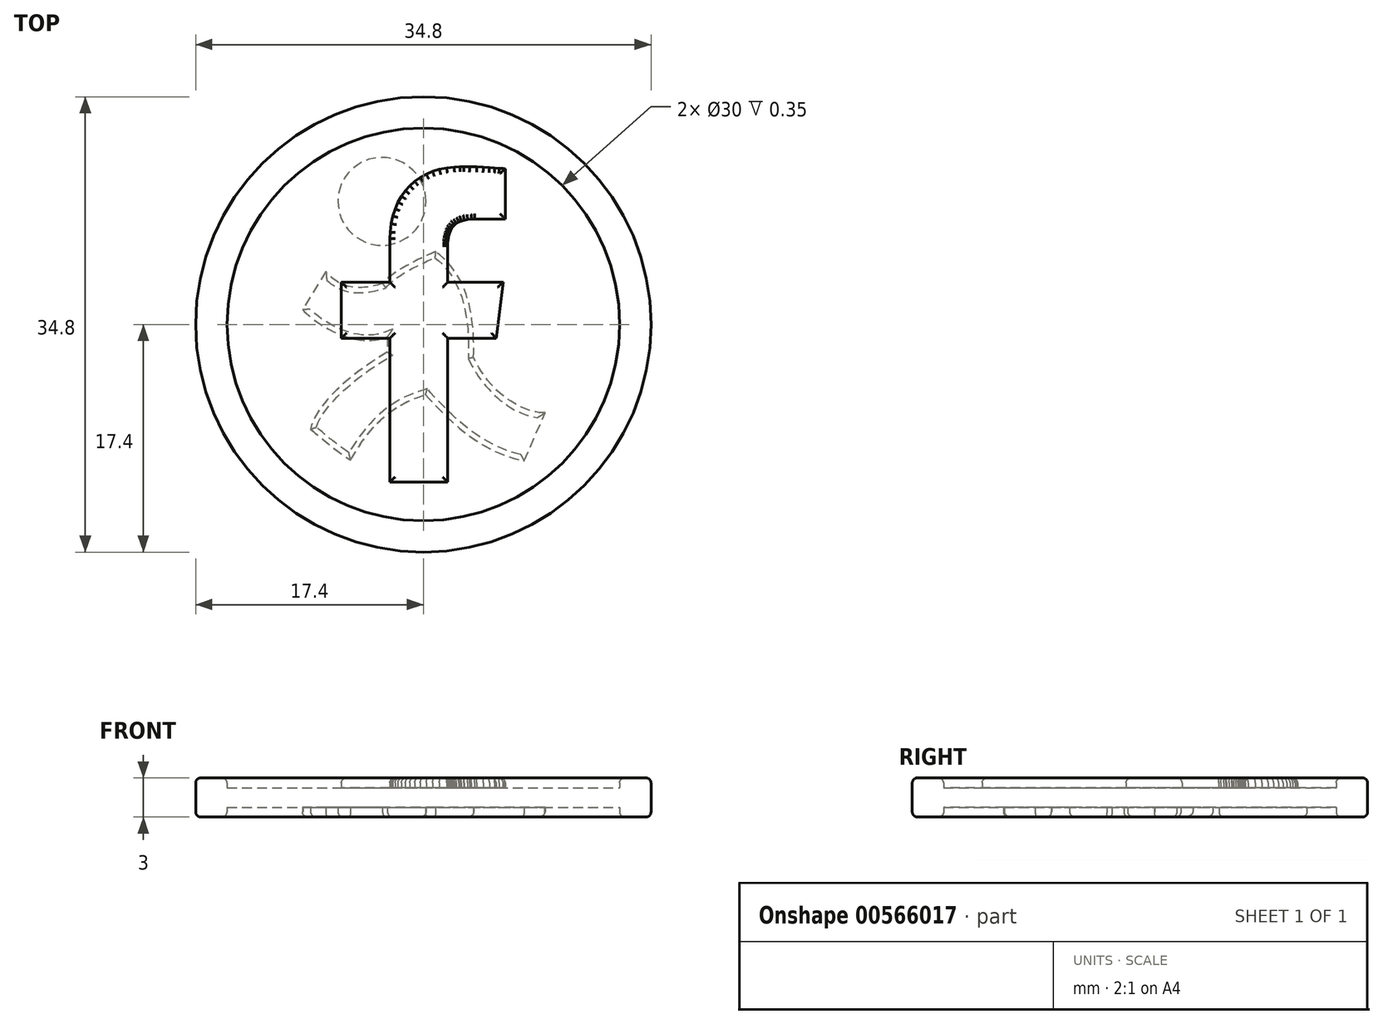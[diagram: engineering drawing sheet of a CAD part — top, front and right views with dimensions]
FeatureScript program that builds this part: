
annotation { "Feature Type Name" : "Feature", "Feature Type Description" : "" }
export const myFeature = defineFeature(function(context is Context, id is Id, definition is map)
    precondition{}
    {
        {
            var Q0;
            Q0=qCreatedBy(makeId("Front.planeOp"),FACE);
            var sketch = newSketch(context, id + "F0", { "sketchPlane" : qUnion([Q0])});
            skLineSegment(sketch, "E0", {"start": v(0, 0) * mm, "end": v(0, 0.75) * mm});
            skLineSegment(sketch, "E1", {"start": v(0, 0.75) * mm, "end": v(-15, 0.75) * mm});
            skLineSegment(sketch, "E2", {"start": v(-15, 0.75) * mm, "end": v(-17.4, 0.75) * mm});
            skLineSegment(sketch, "E3", {"start": v(-17.4, 0.75) * mm, "end": v(-17.4, 0) * mm});
            skLineSegment(sketch, "E4", {"start": v(-17.4, 0) * mm, "end": v(0, 0) * mm});
            skLineSegment(sketch, "E5", {"start": v(-15, 0.75) * mm, "end": v(-15, 0) * mm});
            skLineSegment(sketch, "E6.MirrorCS", {"start": v(0, 0) * mm, "end": v(0, -0.75) * mm});
            skLineSegment(sketch, "E7.MirrorCS", {"start": v(-15, -0.75) * mm, "end": v(-15, 0) * mm});
            skLineSegment(sketch, "E8.MirrorCS", {"start": v(-17.4, -0.75) * mm, "end": v(-17.4, 0) * mm});
            skLineSegment(sketch, "E9.MirrorCS", {"start": v(0, -0.75) * mm, "end": v(-15, -0.75) * mm});
            skLineSegment(sketch, "E10.MirrorCS", {"start": v(-15, -0.75) * mm, "end": v(-17.4, -0.75) * mm});
            skSolve(sketch);
        }
        {
            var Q0;
            {var subQ2=sQuery(id+"F0.wireOp",EDGE,"E7.MirrorCS");Q0=makeQuery(id+"F0.imprint","IMPRINT",FACE,{"disambiguationData":[TD([[makeQuery(id+"F0.imprint","IMPRINT",EDGE,{"derivedFrom":subQ2}),1.0]])]});}
            var Q1;
            Q1=makeQuery(id+"F0.imprint","IMPRINT",FACE,{"disambiguationData":[TD([[makeQuery(id+"F0.imprint","IMPRINT",EDGE,{"derivedFrom":sQuery(id+"F0.wireOp",EDGE,"E2")}),1.0]])]});
            var Q2;
            Q2=sQuery(id+"F0.wireOp",EDGE,"E0");
            revolve(context, id + "F1", {"entities" : qUnion([Q0, Q1]), "axis" : qUnion([Q2]), "revolveType" : RevolveType.FULL});
        }
        {
            var Q0;
            {var subQ0=sQuery(id+"F0.wireOp",EDGE,"E0");Q0=makeQuery(id+"F0.imprint","IMPRINT",FACE,{"disambiguationData":[TD([[makeQuery(id+"F0.imprint","IMPRINT",EDGE,{"derivedFrom":subQ0}),1.0]])]});}
            var Q1;
            {var subQ0=sQuery(id+"F0.wireOp",EDGE,"E6.MirrorCS");Q1=makeQuery(id+"F0.imprint","IMPRINT",FACE,{"disambiguationData":[TD([[makeQuery(id+"F0.imprint","IMPRINT",EDGE,{"derivedFrom":subQ0}),-1.0]])]});}
            var Q2;
            Q2=sQuery(id+"F0.wireOp",EDGE,"E0");
            revolve(context, id + "F2", {"entities" : qUnion([Q0, Q1]), "axis" : qUnion([Q2]), "revolveType" : RevolveType.FULL});
        }
        {
            var Q0;
            Q0=makeQuery(id+"F2.opRevolve","SWEPT_FACE",FACE,{"disambiguationData":[OSD([sQuery(id+"F0.wireOp",EDGE,"E1")])]});
            var sketch = newSketch(context, id + "F3", { "sketchPlane" : qUnion([Q0])});
            skLineSegment(sketch, "E11", {"start": v(1.87, -12.06) * mm, "end": v(1.87, -1.06) * mm});
            skLineSegment(sketch, "E12", {"start": v(1.87, -1.06) * mm, "end": v(5.56, -1.06) * mm});
            skLineSegment(sketch, "E13", {"start": v(5.56, -1.06) * mm, "end": v(6.11, 3.23) * mm});
            skLineSegment(sketch, "E14", {"start": v(6.11, 3.23) * mm, "end": v(1.87, 3.23) * mm});
            skLineSegment(sketch, "E15", {"start": v(1.87, 3.23) * mm, "end": v(1.87, 5.97) * mm});
            skLineSegment(sketch, "E16", {"start": v(1.87, 5.97) * mm, "end": v(1.87, 6.02) * mm});
            skLineSegment(sketch, "E17", {"start": v(1.87, 6.02) * mm, "end": v(1.87, 6.2) * mm});
            skLineSegment(sketch, "E18", {"start": v(1.87, 6.2) * mm, "end": v(1.89, 6.41) * mm});
            skLineSegment(sketch, "E19", {"start": v(1.89, 6.41) * mm, "end": v(1.91, 6.62) * mm});
            skLineSegment(sketch, "E20", {"start": v(1.91, 6.62) * mm, "end": v(1.95, 6.82) * mm});
            skLineSegment(sketch, "E21", {"start": v(1.95, 6.82) * mm, "end": v(2, 7) * mm});
            skLineSegment(sketch, "E22", {"start": v(2, 7) * mm, "end": v(2.07, 7.17) * mm});
            skLineSegment(sketch, "E23", {"start": v(2.07, 7.17) * mm, "end": v(2.16, 7.33) * mm});
            skLineSegment(sketch, "E24", {"start": v(2.16, 7.33) * mm, "end": v(2.26, 7.48) * mm});
            skLineSegment(sketch, "E25", {"start": v(2.26, 7.48) * mm, "end": v(2.39, 7.6) * mm});
            skLineSegment(sketch, "E26", {"start": v(2.39, 7.6) * mm, "end": v(2.54, 7.72) * mm});
            skLineSegment(sketch, "E27", {"start": v(2.54, 7.72) * mm, "end": v(2.71, 7.82) * mm});
            skLineSegment(sketch, "E28", {"start": v(2.71, 7.82) * mm, "end": v(2.9, 7.9) * mm});
            skLineSegment(sketch, "E29", {"start": v(2.9, 7.9) * mm, "end": v(3.13, 7.97) * mm});
            skLineSegment(sketch, "E30", {"start": v(3.13, 7.97) * mm, "end": v(3.39, 8.01) * mm});
            skLineSegment(sketch, "E31", {"start": v(3.39, 8.01) * mm, "end": v(3.67, 8.04) * mm});
            skLineSegment(sketch, "E32", {"start": v(3.67, 8.04) * mm, "end": v(3.91, 8.05) * mm});
            skLineSegment(sketch, "E33", {"start": v(3.91, 8.05) * mm, "end": v(4, 8.05) * mm});
            skLineSegment(sketch, "E34", {"start": v(4, 8.05) * mm, "end": v(6.26, 8.05) * mm});
            skLineSegment(sketch, "E35", {"start": v(6.26, 8.05) * mm, "end": v(6.26, 11.89) * mm});
            skLineSegment(sketch, "E36", {"start": v(6.26, 11.89) * mm, "end": v(6.21, 11.9) * mm});
            skLineSegment(sketch, "E37", {"start": v(6.21, 11.9) * mm, "end": v(6.07, 11.91) * mm});
            skLineSegment(sketch, "E38", {"start": v(6.07, 11.91) * mm, "end": v(5.8, 11.94) * mm});
            skLineSegment(sketch, "E39", {"start": v(5.8, 11.94) * mm, "end": v(5.46, 11.96) * mm});
            skLineSegment(sketch, "E40", {"start": v(5.46, 11.96) * mm, "end": v(5.05, 12) * mm});
            skLineSegment(sketch, "E41", {"start": v(5.05, 12) * mm, "end": v(4.59, 12.02) * mm});
            skLineSegment(sketch, "E42", {"start": v(4.59, 12.02) * mm, "end": v(4.08, 12.04) * mm});
            skLineSegment(sketch, "E43", {"start": v(4.08, 12.04) * mm, "end": v(3.53, 12.05) * mm});
            skLineSegment(sketch, "E44", {"start": v(3.53, 12.05) * mm, "end": v(3.1, 12.06) * mm});
            skLineSegment(sketch, "E45", {"start": v(3.1, 12.06) * mm, "end": v(2.95, 12.06) * mm});
            skLineSegment(sketch, "E46", {"start": v(2.95, 12.06) * mm, "end": v(2.8, 12.06) * mm});
            skLineSegment(sketch, "E47", {"start": v(2.8, 12.06) * mm, "end": v(2.35, 12.03) * mm});
            skLineSegment(sketch, "E48", {"start": v(2.35, 12.03) * mm, "end": v(1.78, 11.96) * mm});
            skLineSegment(sketch, "E49", {"start": v(1.78, 11.96) * mm, "end": v(1.23, 11.85) * mm});
            skLineSegment(sketch, "E50", {"start": v(1.23, 11.85) * mm, "end": v(0.71, 11.69) * mm});
            skLineSegment(sketch, "E51", {"start": v(0.71, 11.69) * mm, "end": v(0.22, 11.48) * mm});
            skLineSegment(sketch, "E52", {"start": v(0.22, 11.48) * mm, "end": v(-0.23, 11.23) * mm});
            skLineSegment(sketch, "E53", {"start": v(-0.23, 11.23) * mm, "end": v(-0.65, 10.94) * mm});
            skLineSegment(sketch, "E54", {"start": v(-0.65, 10.94) * mm, "end": v(-1.03, 10.6) * mm});
            skLineSegment(sketch, "E55", {"start": v(-1.03, 10.6) * mm, "end": v(-1.37, 10.22) * mm});
            skLineSegment(sketch, "E56", {"start": v(-1.37, 10.22) * mm, "end": v(-1.68, 9.8) * mm});
            skLineSegment(sketch, "E57", {"start": v(-1.68, 9.8) * mm, "end": v(-1.94, 9.33) * mm});
            skLineSegment(sketch, "E58", {"start": v(-1.94, 9.33) * mm, "end": v(-2.16, 8.82) * mm});
            skLineSegment(sketch, "E59", {"start": v(-2.16, 8.82) * mm, "end": v(-2.33, 8.28) * mm});
            skLineSegment(sketch, "E60", {"start": v(-2.33, 8.28) * mm, "end": v(-2.46, 7.69) * mm});
            skLineSegment(sketch, "E61", {"start": v(-2.46, 7.69) * mm, "end": v(-2.53, 7.06) * mm});
            skLineSegment(sketch, "E62", {"start": v(-2.53, 7.06) * mm, "end": v(-2.56, 6.56) * mm});
            skLineSegment(sketch, "E63", {"start": v(-2.56, 6.56) * mm, "end": v(-2.56, 6.4) * mm});
            skLineSegment(sketch, "E64", {"start": v(-2.56, 6.4) * mm, "end": v(-2.56, 3.23) * mm});
            skLineSegment(sketch, "E65", {"start": v(-2.56, 3.23) * mm, "end": v(-6.26, 3.23) * mm});
            skLineSegment(sketch, "E66", {"start": v(-6.26, 3.23) * mm, "end": v(-6.26, -1.06) * mm});
            skLineSegment(sketch, "E67", {"start": v(-6.26, -1.06) * mm, "end": v(-2.56, -1.06) * mm});
            skLineSegment(sketch, "E68", {"start": v(-2.56, -1.06) * mm, "end": v(-2.56, -12.06) * mm});
            skLineSegment(sketch, "E69", {"start": v(-2.56, -12.06) * mm, "end": v(1.87, -12.06) * mm});
            skSolve(sketch);
        }
        {
            var Q0;
            Q0=makeQuery(id+"F2.opRevolve","SWEPT_FACE",FACE,{"disambiguationData":[OSD([sQuery(id+"F0.wireOp",EDGE,"E9.MirrorCS")])]});
            var sketch = newSketch(context, id + "F4", { "sketchPlane" : qUnion([Q0])});
            skFitSpline(sketch, "E70", {"points": [v(0.93, -5.57) * mm, v(-3.11, -3.13) * mm], "startDerivative": vector(-3.58, 1.6) * mm, "endDerivative": vector(-2.6, 3.06) * mm});
            skFitSpline(sketch, "E71", {"points": [v(-3.11, -3.13) * mm, v(-7.44, -4.04) * mm], "startDerivative": vector(-6.77, 2.16) * mm, "endDerivative": vector(-2.52, -3.04) * mm});
            skFitSpline(sketch, "E72", {"points": [v(-7.44, -4.04) * mm, v(-9.24, -1.13) * mm], "startDerivative": vector(-1.8, 2.9) * mm, "endDerivative": vector(-1.8, 2.9) * mm});
            skFitSpline(sketch, "E73", {"points": [v(-9.2, -1.1) * mm, v(-2.74, 0.94) * mm], "startDerivative": vector(2.37, 2.47) * mm, "endDerivative": vector(8.3, -3.22) * mm});
            skPoint(sketch, "E74", {"position": v(-8.25, -0.28) * mm});
            skFitSpline(sketch, "E75", {"points": [v(-2.74, 0.94) * mm, v(-2.74, 2.12) * mm], "startDerivative": vector(0, 1.18) * mm, "endDerivative": vector(0, 1.18) * mm});
            skFitSpline(sketch, "E76", {"points": [v(-2.74, 2.12) * mm, v(-8.62, 8) * mm], "startDerivative": vector(-6.87, 3.99) * mm, "endDerivative": vector(-1.37, 6.4) * mm});
            skFitSpline(sketch, "E77", {"points": [v(-8.62, 8) * mm, v(-5.56, 10.36) * mm], "startDerivative": vector(2.5, 2.07) * mm, "endDerivative": vector(3.24, 2) * mm});
            skFitSpline(sketch, "E78", {"points": [v(-5.56, 10.36) * mm, v(0.17, 5.37) * mm], "startDerivative": vector(3.77, -6.34) * mm, "endDerivative": vector(9.12, -2.66) * mm});
            skFitSpline(sketch, "E79", {"points": [v(0.17, 5.37) * mm, v(7.71, 10.43) * mm], "startDerivative": vector(6.57, 7.32) * mm, "endDerivative": vector(9.36, 1.87) * mm});
            skFitSpline(sketch, "E80", {"points": [v(7.71, 10.43) * mm, v(9.3, 6.76) * mm], "startDerivative": vector(1.6, -3.67) * mm, "endDerivative": vector(1.6, -3.67) * mm});
            skFitSpline(sketch, "E81", {"points": [v(9.27, 6.76) * mm, v(3.83, 2.53) * mm], "startDerivative": vector(-4.54, 0.03) * mm, "endDerivative": vector(-4.44, -9.07) * mm});
            skFitSpline(sketch, "E82", {"points": [v(3.83, 2.53) * mm, v(0.93, -5.57) * mm], "startDerivative": vector(0.3, -9.93) * mm, "endDerivative": vector(-7.4, -5.39) * mm});
            skCircle(sketch, "E83", {"center": v(-3.16, -9.4) * mm, "radius": 3.36 * mm});
            skPoint(sketch, "E83.first.point", {"position": v(-3.02, -12.76) * mm});
            skPoint(sketch, "E83.second.point", {"position": v(-3.35, -6.05) * mm});
            skPoint(sketch, "E83.third.point", {"position": v(-6.12, -7.81) * mm});
            skLineSegment(sketch, "E84", {"start": v(-9.24, -1.13) * mm, "end": v(-9.2, -1.1) * mm});
            skLineSegment(sketch, "E85", {"start": v(9.3, 6.76) * mm, "end": v(9.27, 6.76) * mm});
            skSolve(sketch);
        }
        {
            var Q0;
            Q0=makeQuery(id+"F3.imprint","IMPRINT",FACE,{"disambiguationData":[TD([[makeQuery(id+"F3.imprint","IMPRINT",EDGE,{"derivedFrom":sQuery(id+"F3.wireOp",EDGE,"E11")}),1.0]])]});
            var Q1;
            Q1=makeQuery(id+"F1.opRevolve","SWEPT_FACE",FACE,{"disambiguationData":[OSD([sQuery(id+"F0.wireOp",EDGE,"E2")])]});
            var Q2;
            Q2=makeQuery(id+"F1.opRevolve","SWEPT_FACE",FACE,{"disambiguationData":[OSD([sQuery(id+"F0.wireOp",EDGE,"E10.MirrorCS")])]});
            var Q3;
            Q3=makeQuery(id+"F4.imprint","IMPRINT",FACE,{"disambiguationData":[TD([[makeQuery(id+"F4.imprint","IMPRINT",EDGE,{"derivedFrom":sQuery(id+"F4.wireOp",EDGE,"E83")}),1.0]])]});
            var Q4;
            Q4=makeQuery(id+"F4.imprint","IMPRINT",FACE,{"disambiguationData":[TD([[makeQuery(id+"F4.imprint","IMPRINT",EDGE,{"derivedFrom":sQuery(id+"F4.wireOp",EDGE,"E70")}),-1.0]])]});
            extrude(context, id + "F5", {"entities" : qUnion([Q0, Q1, Q2, Q3, Q4]), "operationType" : NewBodyOperationType.ADD, "endBound" : BoundingType.SYMMETRIC, "depth" : 1.5 * mm, "offsetDistance" : 25 * mm});
        }
        {
            var Q0;
            Q0=makeQuery(id+"F5.opExtrude","CAP_FACE",FACE,{"disambiguationData":[OSD([sQuery(id+"F0.wireOp",EDGE,"E10.MirrorCS")])],"isStart":true});
            var Q1;
            Q1=makeQuery(id+"F5.opExtrude","CAP_FACE",FACE,{"disambiguationData":[OSD([sQuery(id+"F0.wireOp",EDGE,"E2")])],"isStart":false});
            var Q2;
            Q2=makeQuery(id+"F5.opExtrude","CAP_FACE",FACE,{"disambiguationData":[OSD([sQuery(id+"F4.wireOp",EDGE,"E70"),sQuery(id+"F4.wireOp",EDGE,"E71"),sQuery(id+"F4.wireOp",EDGE,"E72"),sQuery(id+"F4.wireOp",EDGE,"E73"),sQuery(id+"F4.wireOp",EDGE,"E75"),sQuery(id+"F4.wireOp",EDGE,"E76"),sQuery(id+"F4.wireOp",EDGE,"E77"),sQuery(id+"F4.wireOp",EDGE,"E78"),sQuery(id+"F4.wireOp",EDGE,"E79"),sQuery(id+"F4.wireOp",EDGE,"E80"),sQuery(id+"F4.wireOp",EDGE,"E81"),sQuery(id+"F4.wireOp",EDGE,"E82"),sQuery(id+"F4.wireOp",EDGE,"E84"),sQuery(id+"F4.wireOp",EDGE,"E85")])],"isStart":true});
            var Q3;
            Q3=makeQuery(id+"F5.opExtrude","CAP_FACE",FACE,{"disambiguationData":[OSD([sQuery(id+"F4.wireOp",EDGE,"E83")])],"isStart":true});
            var Q4;
            Q4=makeQuery(id+"F5.opExtrude","CAP_FACE",FACE,{"disambiguationData":[OSD([sQuery(id+"F3.wireOp",EDGE,"E11"),sQuery(id+"F3.wireOp",EDGE,"E12"),sQuery(id+"F3.wireOp",EDGE,"E13"),sQuery(id+"F3.wireOp",EDGE,"E14"),sQuery(id+"F3.wireOp",EDGE,"E15"),sQuery(id+"F3.wireOp",EDGE,"E16"),sQuery(id+"F3.wireOp",EDGE,"E17"),sQuery(id+"F3.wireOp",EDGE,"E18"),sQuery(id+"F3.wireOp",EDGE,"E19"),sQuery(id+"F3.wireOp",EDGE,"E20"),sQuery(id+"F3.wireOp",EDGE,"E21"),sQuery(id+"F3.wireOp",EDGE,"E22"),sQuery(id+"F3.wireOp",EDGE,"E23"),sQuery(id+"F3.wireOp",EDGE,"E24"),sQuery(id+"F3.wireOp",EDGE,"E25"),sQuery(id+"F3.wireOp",EDGE,"E26"),sQuery(id+"F3.wireOp",EDGE,"E27"),sQuery(id+"F3.wireOp",EDGE,"E28"),sQuery(id+"F3.wireOp",EDGE,"E29"),sQuery(id+"F3.wireOp",EDGE,"E30"),sQuery(id+"F3.wireOp",EDGE,"E31"),sQuery(id+"F3.wireOp",EDGE,"E32"),sQuery(id+"F3.wireOp",EDGE,"E33"),sQuery(id+"F3.wireOp",EDGE,"E34"),sQuery(id+"F3.wireOp",EDGE,"E35"),sQuery(id+"F3.wireOp",EDGE,"E36"),sQuery(id+"F3.wireOp",EDGE,"E37"),sQuery(id+"F3.wireOp",EDGE,"E38"),sQuery(id+"F3.wireOp",EDGE,"E39"),sQuery(id+"F3.wireOp",EDGE,"E40"),sQuery(id+"F3.wireOp",EDGE,"E41"),sQuery(id+"F3.wireOp",EDGE,"E42"),sQuery(id+"F3.wireOp",EDGE,"E43"),sQuery(id+"F3.wireOp",EDGE,"E44"),sQuery(id+"F3.wireOp",EDGE,"E45"),sQuery(id+"F3.wireOp",EDGE,"E46"),sQuery(id+"F3.wireOp",EDGE,"E47"),sQuery(id+"F3.wireOp",EDGE,"E48"),sQuery(id+"F3.wireOp",EDGE,"E49"),sQuery(id+"F3.wireOp",EDGE,"E50"),sQuery(id+"F3.wireOp",EDGE,"E51"),sQuery(id+"F3.wireOp",EDGE,"E52"),sQuery(id+"F3.wireOp",EDGE,"E53"),sQuery(id+"F3.wireOp",EDGE,"E54"),sQuery(id+"F3.wireOp",EDGE,"E55"),sQuery(id+"F3.wireOp",EDGE,"E56"),sQuery(id+"F3.wireOp",EDGE,"E57"),sQuery(id+"F3.wireOp",EDGE,"E58"),sQuery(id+"F3.wireOp",EDGE,"E59"),sQuery(id+"F3.wireOp",EDGE,"E60"),sQuery(id+"F3.wireOp",EDGE,"E61"),sQuery(id+"F3.wireOp",EDGE,"E62"),sQuery(id+"F3.wireOp",EDGE,"E63"),sQuery(id+"F3.wireOp",EDGE,"E64"),sQuery(id+"F3.wireOp",EDGE,"E65"),sQuery(id+"F3.wireOp",EDGE,"E66"),sQuery(id+"F3.wireOp",EDGE,"E67"),sQuery(id+"F3.wireOp",EDGE,"E68"),sQuery(id+"F3.wireOp",EDGE,"E69")])],"isStart":false});
            fillet(context, id + "F6", {"entities" : qUnion([Q0, Q1, Q2, Q3, Q4]), "radius" : 0.4 * mm, "tangentPropagation" : true, "allowEdgeOverflow" : false});
        }
    });
